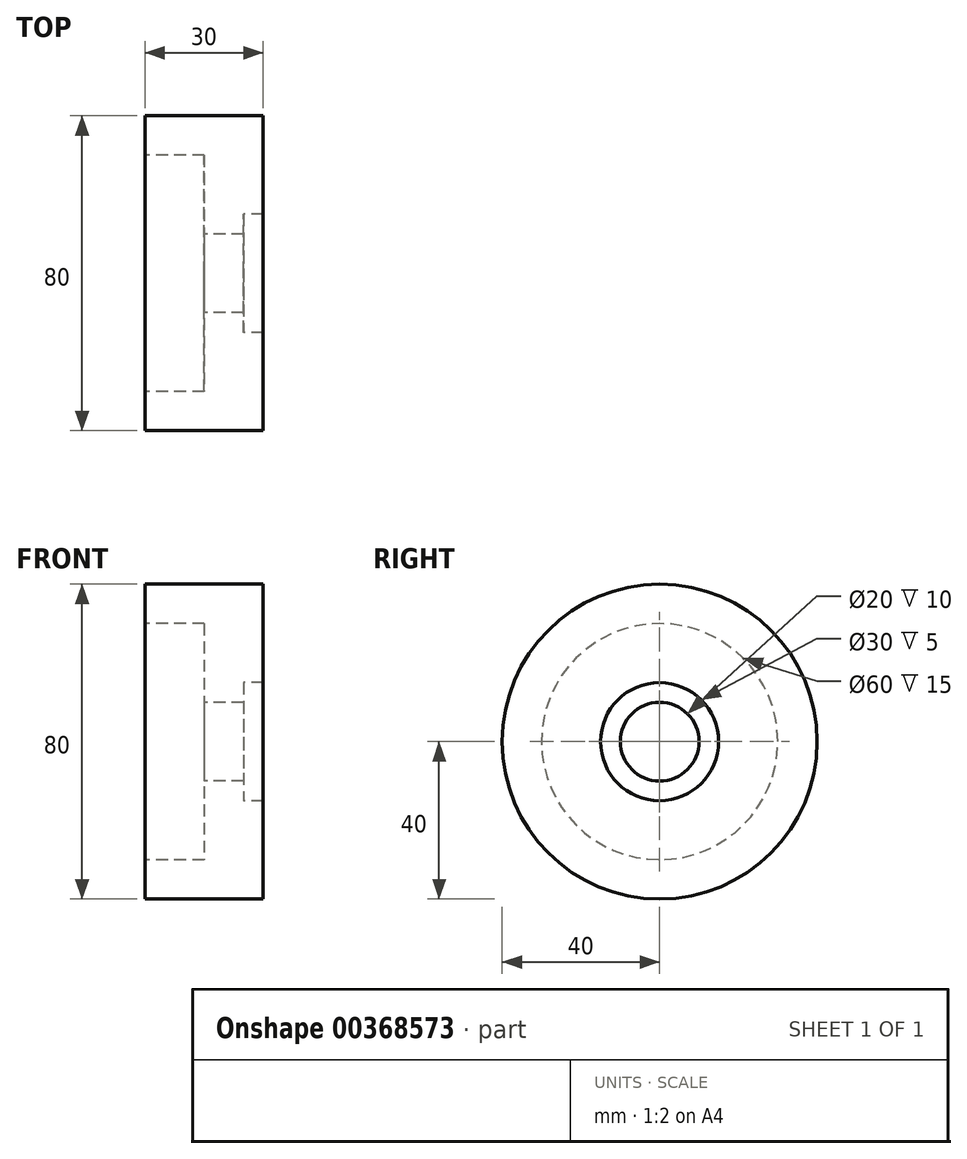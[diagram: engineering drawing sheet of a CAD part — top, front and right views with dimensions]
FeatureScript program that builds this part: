
annotation { "Feature Type Name" : "Feature", "Feature Type Description" : "" }
export const myFeature = defineFeature(function(context is Context, id is Id, definition is map)
    precondition{}
    {
        {
            var Q0;
            Q0=qCreatedBy(makeId("Front.planeOp"),FACE);
            var sketch = newSketch(context, id + "F0", { "sketchPlane" : qUnion([Q0])});
            skLineSegment(sketch, "E0", {"start": v(0, 10) * mm, "end": v(10, 10) * mm});
            skLineSegment(sketch, "E1", {"start": v(10, 10) * mm, "end": v(10, 15) * mm});
            skLineSegment(sketch, "E2", {"start": v(10, 15) * mm, "end": v(15, 15) * mm});
            skLineSegment(sketch, "E3", {"start": v(15, 15) * mm, "end": v(15, 40) * mm});
            skLineSegment(sketch, "E4", {"start": v(15, 40) * mm, "end": v(-15, 40) * mm});
            skLineSegment(sketch, "E5", {"start": v(-15, 40) * mm, "end": v(-15, 30) * mm});
            skLineSegment(sketch, "E6", {"start": v(-15, 30) * mm, "end": v(0, 30) * mm});
            skLineSegment(sketch, "E7", {"start": v(0, 30) * mm, "end": v(0, 10) * mm});
            skLineSegment(sketch, "E8", {"start": v(0, 0) * mm, "end": v(26.23, 0) * mm});
            skSolve(sketch);
        }
        {
            var Q0;
            Q0=makeQuery(id+"F0.imprint","IMPRINT",FACE,{"disambiguationData":[TD([[makeQuery(id+"F0.imprint","IMPRINT",EDGE,{"derivedFrom":sQuery(id+"F0.wireOp",EDGE,"E0")}),1.0]])]});
            var Q1;
            Q1=sQuery(id+"F0.wireOp",EDGE,"E8");
            revolve(context, id + "F1", {"entities" : qUnion([Q0]), "axis" : qUnion([Q1]), "revolveType" : RevolveType.FULL});
        }
    });
